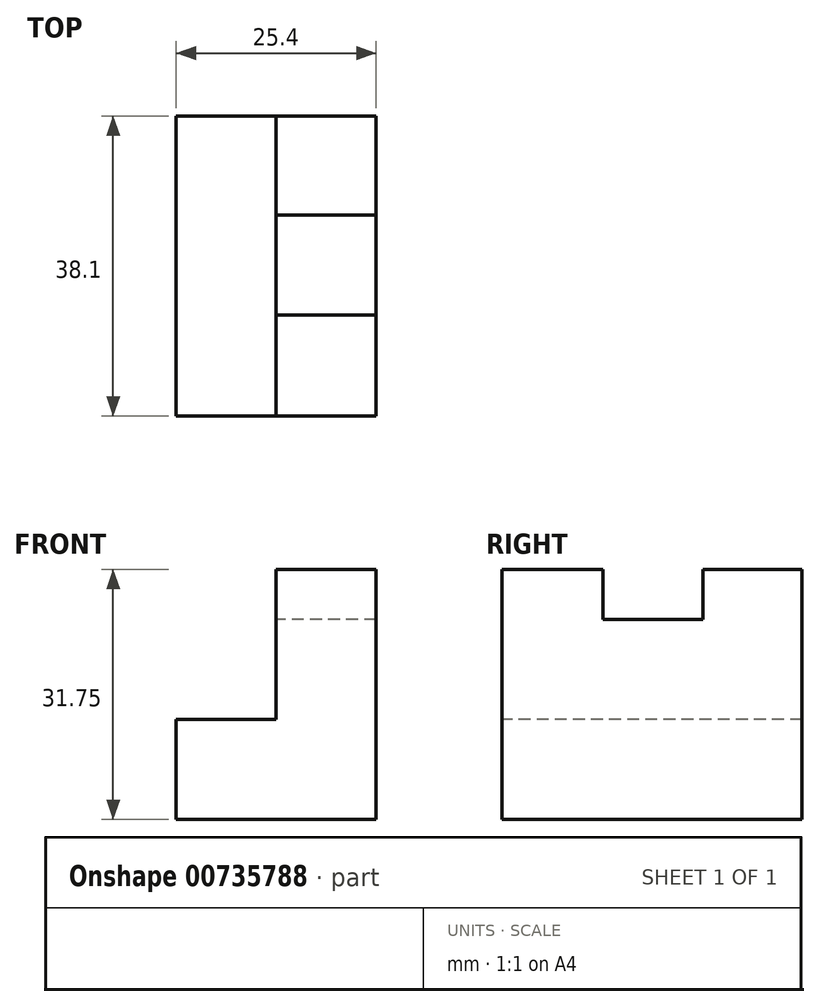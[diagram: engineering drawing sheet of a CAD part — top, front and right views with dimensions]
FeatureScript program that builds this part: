
annotation { "Feature Type Name" : "Feature", "Feature Type Description" : "" }
export const myFeature = defineFeature(function(context is Context, id is Id, definition is map)
    precondition{}
    {
        {
            var Q0;
            Q0=qCreatedBy(makeId("Front.planeOp"),FACE);
            var sketch = newSketch(context, id + "F0", { "sketchPlane" : qUnion([Q0])});
            skLineSegment(sketch, "E0", {"start": v(0, 0) * mm, "end": v(25.4, 0) * mm});
            skLineSegment(sketch, "E1", {"start": v(25.4, 0) * mm, "end": v(25.4, 31.75) * mm});
            skLineSegment(sketch, "E2", {"start": v(25.4, 31.75) * mm, "end": v(12.7, 31.75) * mm});
            skLineSegment(sketch, "E3", {"start": v(12.7, 31.75) * mm, "end": v(12.7, 12.7) * mm});
            skLineSegment(sketch, "E4", {"start": v(12.7, 12.7) * mm, "end": v(0, 12.7) * mm});
            skLineSegment(sketch, "E5", {"start": v(0, 12.7) * mm, "end": v(0, 0) * mm});
            skSolve(sketch);
        }
        {
            var Q0;
            Q0 = qSketchRegion(id + "F0", true);
            extrude(context, id + "F1", {"entities" : qUnion([Q0]), "oppositeDirection" : true, "depth" : 38.1 * mm, "offsetDistance" : 25.4 * mm});
        }
        {
            var Q0;
            Q0=makeQuery(id+"F1.opExtrude","SWEPT_FACE",FACE,{"disambiguationData":[OSD([sQuery(id+"F0.wireOp",EDGE,"E3")])]});
            var sketch = newSketch(context, id + "F2", { "sketchPlane" : qUnion([Q0])});
            skLineSegment(sketch, "E6", {"start": v(-25.5, 31.75) * mm, "end": v(-25.5, 25.4) * mm});
            skLineSegment(sketch, "E7", {"start": v(-25.5, 25.4) * mm, "end": v(-12.8, 25.4) * mm});
            skLineSegment(sketch, "E8", {"start": v(-12.8, 25.4) * mm, "end": v(-12.8, 31.75) * mm});
            skLineSegment(sketch, "E9", {"start": v(-12.8, 31.75) * mm, "end": v(-25.5, 31.75) * mm});
            skSolve(sketch);
        }
        {
            var Q0;
            Q0=makeQuery(id+"F2.imprint","IMPRINT",FACE,{"disambiguationData":[TD([[makeQuery(id+"F2.imprint","IMPRINT",EDGE,{"derivedFrom":sQuery(id+"F2.wireOp",EDGE,"E6")}),1.0]])]});
            extrude(context, id + "F3", {"entities" : qUnion([Q0]), "operationType" : NewBodyOperationType.REMOVE, "oppositeDirection" : true, "depth" : 12.7 * mm, "offsetDistance" : 25.4 * mm});
        }
    });
